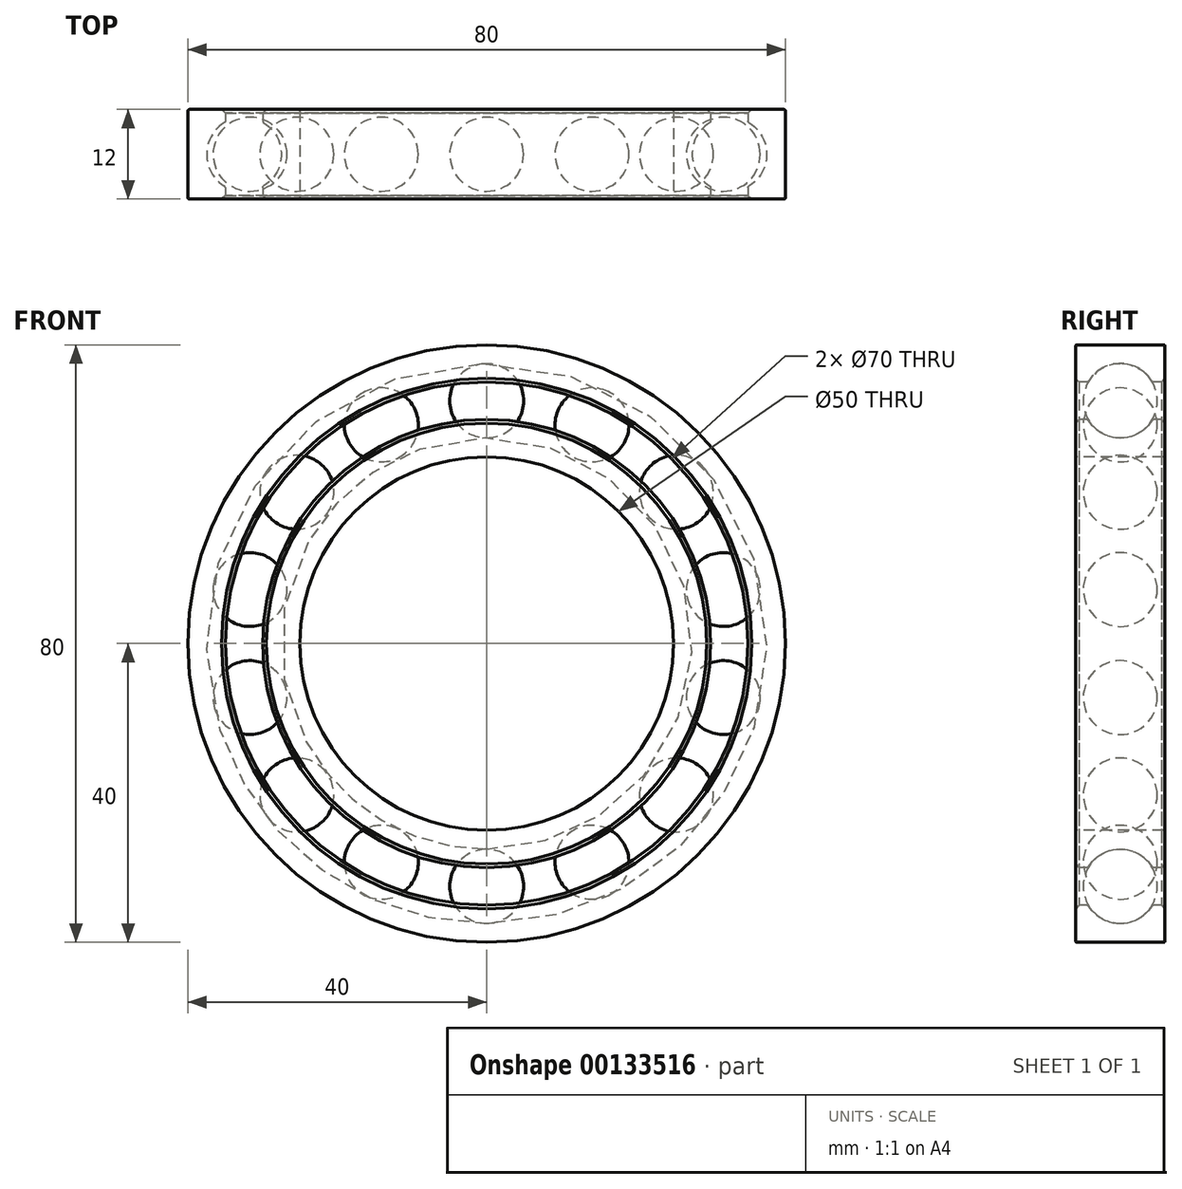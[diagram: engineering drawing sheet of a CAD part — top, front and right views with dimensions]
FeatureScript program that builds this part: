
annotation { "Feature Type Name" : "Feature", "Feature Type Description" : "" }
export const myFeature = defineFeature(function(context is Context, id is Id, definition is map)
    precondition{}
    {
        {
            var Q0;
            Q0=qCreatedBy(makeId("Right.planeOp"),FACE);
            var sketch = newSketch(context, id + "F0", { "sketchPlane" : qUnion([Q0])});
            skLineSegment(sketch, "E0.bottom", {"start": v(-6, 40) * mm, "end": v(6, 40) * mm});
            skLineSegment(sketch, "E0.top", {"start": v(-6, 25) * mm, "end": v(6, 25) * mm});
            skLineSegment(sketch, "E0.left", {"start": v(-6, 40) * mm, "end": v(-6, 35) * mm});
            skLineSegment(sketch, "E0.right", {"start": v(6, 40) * mm, "end": v(6, 35) * mm});
            skLineSegment(sketch, "E1.bottom", {"start": v(-6, 35) * mm, "end": v(-4.33, 35) * mm});
            skLineSegment(sketch, "E1.top", {"start": v(-6, 30) * mm, "end": v(-4.33, 30) * mm});
            skArc(sketch, "E2", {"start": v(-4.33, 30) * mm, "mid": v(0, 27.5) * mm, "end": v(4.33, 30) * mm});
            skPoint(sketch, "E2.centerSnap0", {"position": v(-6, 32.5) * mm});
            skLineSegment(sketch, "E3", {"start": v(16, 32.5) * mm, "end": v(-14.25, 32.5) * mm, "construction": true});
            skLineSegment(sketch, "E4.trimOffspring", {"start": v(-6, 30) * mm, "end": v(-6, 25) * mm});
            skLineSegment(sketch, "E5.trimOffspring", {"start": v(4.33, 35) * mm, "end": v(6, 35) * mm});
            skLineSegment(sketch, "E6.trimOffspring", {"start": v(4.33, 30) * mm, "end": v(6, 30) * mm});
            skArc(sketch, "E7.trimOffspring", {"start": v(4.33, 35) * mm, "mid": v(0, 37.5) * mm, "end": v(-4.33, 35) * mm});
            skLineSegment(sketch, "E8.trimOffspring", {"start": v(6, 30) * mm, "end": v(6, 25) * mm});
            skLineSegment(sketch, "E9", {"start": v(0, 0) * mm, "end": v(63.65, 0) * mm, "construction": true});
            skSolve(sketch);
        }
        {
            var Q0;
            Q0 = qSketchRegion(id + "F0", true);
            var Q1;
            Q1=sQuery(id+"F0.wireOp",EDGE,"E9");
            revolve(context, id + "F1", {"entities" : qUnion([Q0]), "axis" : qUnion([Q1]), "revolveType" : RevolveType.FULL});
        }
        {
            var Q0;
            Q0=makeQuery(id+"F1.opRevolve","SWEPT_FACE",FACE,{"disambiguationData":[OSD([sQuery(id+"F0.wireOp",EDGE,"E0.bottom")])]});
            var Q1;
            Q1=makeQuery(id+"F1.opRevolve","SWEPT_FACE",FACE,{"disambiguationData":[OSD([sQuery(id+"F0.wireOp",EDGE,"E0.top")])]});
            var Q2;
            Q2=makeQuery(id+"F1.opRevolve","SWEPT_FACE",FACE,{"disambiguationData":[OSD([sQuery(id+"F0.wireOp",EDGE,"E7.trimOffspring")])]});
            var Q3;
            Q3=makeQuery(id+"F1.opRevolve","SWEPT_FACE",FACE,{"disambiguationData":[OSD([sQuery(id+"F0.wireOp",EDGE,"E2")])]});
            fillet(context, id + "F2", {"entities" : qUnion([Q0, Q1, Q2, Q3]), "radius" : 0.2 * mm, "tangentPropagation" : true, "allowEdgeOverflow" : false});
        }
        {
            var Q0;
            Q0=makeQuery(id+"F1.opRevolve","SWEPT_EDGE",EDGE,{"disambiguationData":[OSD([sQuery(id+"F0.wireOp",EDGE,"E0.right"),sQuery(id+"F0.wireOp",EDGE,"E5.trimOffspring")])]});
            var Q1;
            Q1=makeQuery(id+"F1.opRevolve","SWEPT_EDGE",EDGE,{"disambiguationData":[OSD([sQuery(id+"F0.wireOp",EDGE,"E6.trimOffspring"),sQuery(id+"F0.wireOp",EDGE,"E8.trimOffspring")])]});
            var Q2;
            Q2=makeQuery(id+"F1.opRevolve","SWEPT_EDGE",EDGE,{"disambiguationData":[OSD([sQuery(id+"F0.wireOp",EDGE,"E1.top"),sQuery(id+"F0.wireOp",EDGE,"E4.trimOffspring")])]});
            var Q3;
            Q3=makeQuery(id+"F1.opRevolve","SWEPT_EDGE",EDGE,{"disambiguationData":[OSD([sQuery(id+"F0.wireOp",EDGE,"E0.left"),sQuery(id+"F0.wireOp",EDGE,"E1.bottom")])]});
            chamfer(context, id + "F3", {"entities" : qUnion([Q0, Q1, Q2, Q3]), "width" : 0.5 * mm, "tangentPropagation" : true});
        }
        {
            var Q0;
            Q0=qCreatedBy(makeId("Right.planeOp"),FACE);
            var sketch = newSketch(context, id + "F4", { "sketchPlane" : qUnion([Q0])});
            skArc(sketch, "E10", {"start": v(0, 27.55) * mm, "mid": v(4.95, 32.5) * mm, "end": v(0, 37.45) * mm});
            skLineSegment(sketch, "E11", {"start": v(0, 37.45) * mm, "end": v(0, 27.55) * mm});
            skPoint(sketch, "E12.orphan", {"position": v(0, 45.03) * mm});
            skSolve(sketch);
        }
        {
            var Q0;
            Q0=makeQuery(id+"F4.imprint","IMPRINT",FACE,{"disambiguationData":[TD([[makeQuery(id+"F4.imprint","IMPRINT",EDGE,{"derivedFrom":sQuery(id+"F4.wireOp",EDGE,"E10")}),1.0]])]});
            var Q1;
            Q1=sQuery(id+"F4.wireOp",EDGE,"E11");
            revolve(context, id + "F5", {"entities" : qUnion([Q0]), "axis" : qUnion([Q1]), "revolveType" : RevolveType.FULL});
        }
        {
            var Q0;
            Q0=makeQuery(id+"F5.opRevolve","SWEPT_BODY",BODY,{"disambiguationData":[OSD([sQuery(id+"F4.wireOp",EDGE,"E10"),sQuery(id+"F4.wireOp",EDGE,"E11")])]});
            var Q1;
            Q1=makeQuery(id+"F1.opRevolve","SWEPT_FACE",FACE,{"disambiguationData":[OSD([sQuery(id+"F0.wireOp",EDGE,"E0.top")])]});
            circularPattern(context, id + "F6", {"entities" : qUnion([Q0]), "axis" : qUnion([Q1]), "angle" : 360 * degree, "instanceCount" : 14, "equalSpace" : true});
        }
    });
